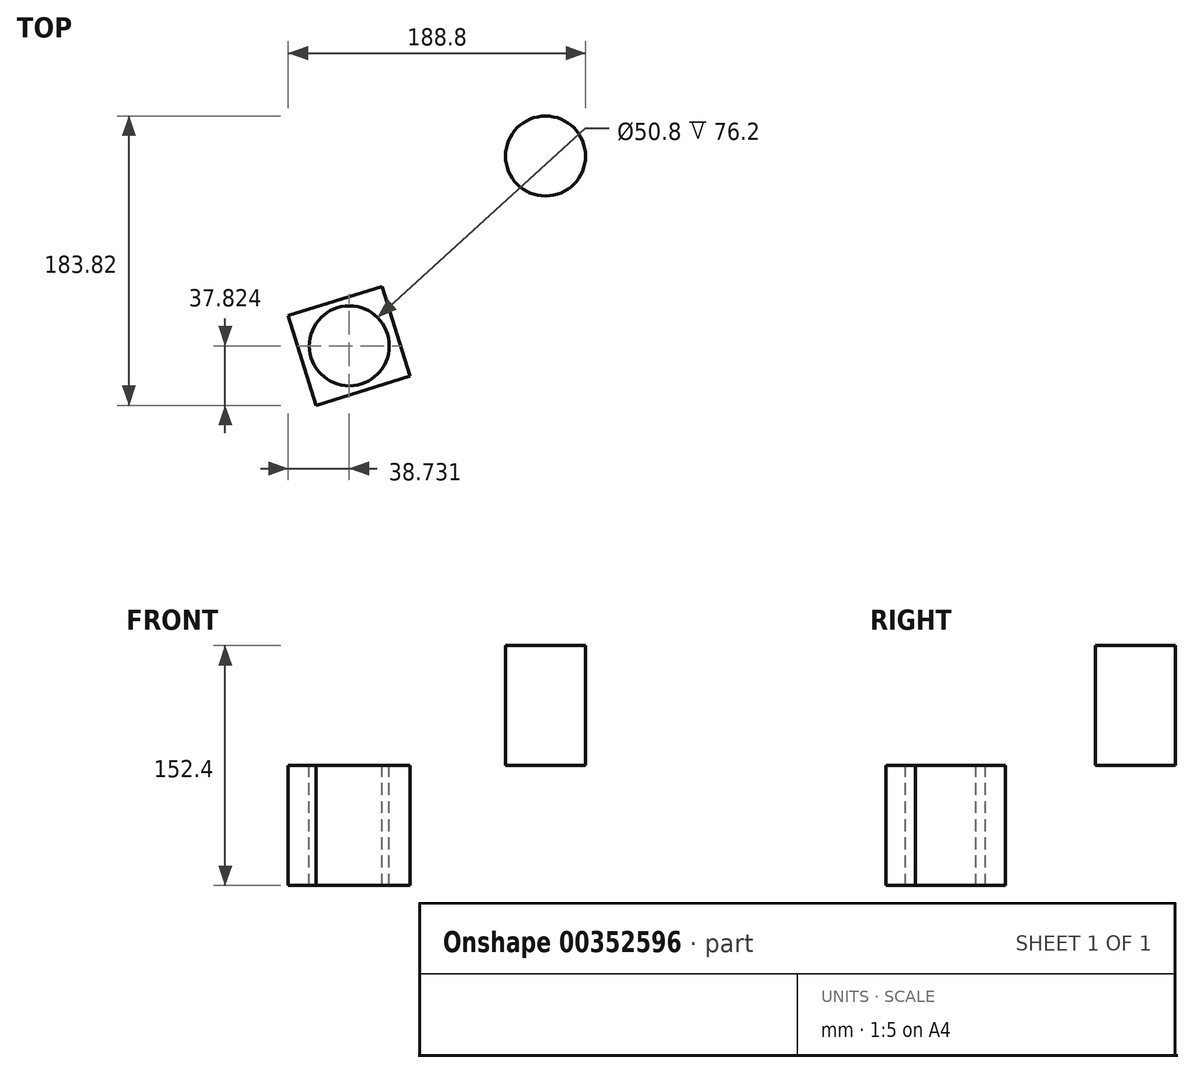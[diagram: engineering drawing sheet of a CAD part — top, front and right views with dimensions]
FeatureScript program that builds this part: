
annotation { "Feature Type Name" : "Feature", "Feature Type Description" : "" }
export const myFeature = defineFeature(function(context is Context, id is Id, definition is map)
    precondition{}
    {
        {
            var Q0;
            Q0=qCreatedBy(makeId("Top.planeOp"),FACE);
            var sketch = newSketch(context, id + "F0", { "sketchPlane" : qUnion([Q0])});
            skCircle(sketch, "E0", {"center": v(-107.28, -18.45) * mm, "radius": 25.4 * mm});
            skSolve(sketch);
        }
        {
            var Q0;
            Q0 = qSketchRegion(id + "F0", true);
            extrude(context, id + "F1", {"entities" : qUnion([Q0]), "depth" : 76.2 * mm});
        }
        {
            var Q0;
            Q0=qCreatedBy(makeId("Top.planeOp"),FACE);
            var sketch = newSketch(context, id + "F2", { "sketchPlane" : qUnion([Q0])});
            skCircle(sketch, "E1", {"center": v(-231.95, -139.05) * mm, "radius": 25.4 * mm});
            skLineSegment(sketch, "E2.bottom", {"start": v(-270.68, -119.89) * mm, "end": v(-211, -101.22) * mm});
            skLineSegment(sketch, "E2.top", {"start": v(-252.9, -176.87) * mm, "end": v(-193.21, -158.2) * mm});
            skLineSegment(sketch, "E2.left", {"start": v(-270.68, -119.89) * mm, "end": v(-252.9, -176.87) * mm});
            skLineSegment(sketch, "E2.right", {"start": v(-211, -101.22) * mm, "end": v(-193.21, -158.2) * mm});
            skLineSegment(sketch, "E3", {"start": v(-240.84, -110.56) * mm, "end": v(-223.06, -167.54) * mm, "construction": true});
            skLineSegment(sketch, "E4", {"start": v(-261.8, -148.38) * mm, "end": v(-202.1, -129.71) * mm, "construction": true});
            skSolve(sketch);
        }
        {
            var Q0;
            Q0=makeQuery(id+"F2.imprint","IMPRINT",FACE,{"disambiguationData":[TD([[makeQuery(id+"F2.imprint","IMPRINT",EDGE,{"derivedFrom":sQuery(id+"F2.wireOp",EDGE,"E1")}),-1.0]])]});
            extrude(context, id + "F3", {"entities" : qUnion([Q0]), "oppositeDirection" : true, "depth" : 76.2 * mm});
        }
    });
